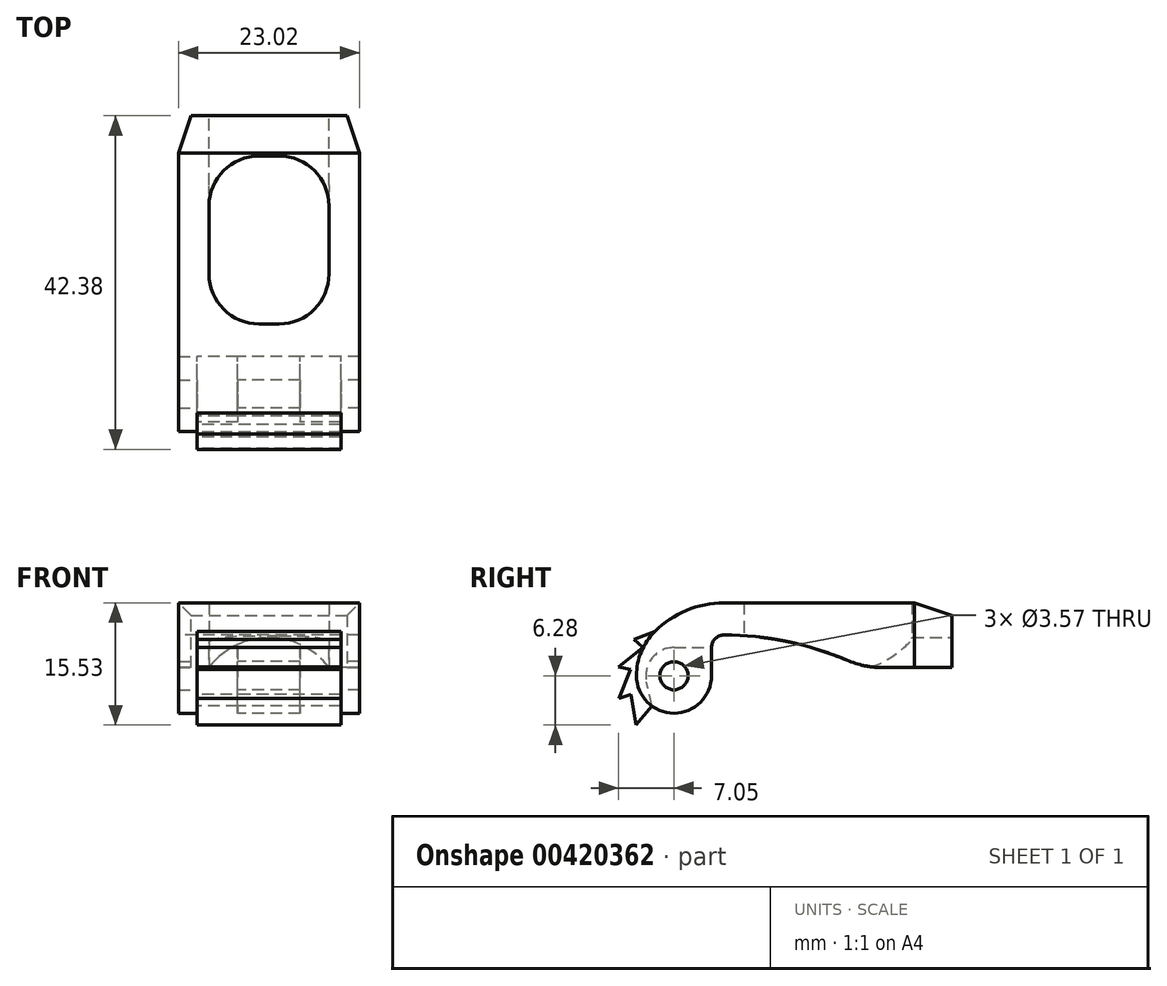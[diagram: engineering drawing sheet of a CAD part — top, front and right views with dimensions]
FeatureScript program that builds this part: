
annotation { "Feature Type Name" : "Feature", "Feature Type Description" : "" }
export const myFeature = defineFeature(function(context is Context, id is Id, definition is map)
    precondition{}
    {
        {
            var Q0;
            Q0=qCreatedBy(makeId("Right.planeOp"),FACE);
            var sketch = newSketch(context, id + "F0", { "sketchPlane" : qUnion([Q0])});
            skCircle(sketch, "E0", {"center": v(0, 0) * mm, "radius": 1.59 * mm, "construction": true});
            skCircle(sketch, "E1", {"center": v(0, 0) * mm, "radius": 1.79 * mm});
            skArc(sketch, "E2", {"start": v(-4.76, 0) * mm, "mid": v(0, -4.76) * mm, "end": v(4.76, 0) * mm});
            skArc(sketch, "E3", {"start": v(-4.76, 0) * mm, "mid": v(-4.16, 3.04) * mm, "end": v(-2.44, 5.61) * mm});
            skArc(sketch, "E4", {"start": v(-2.44, 5.61) * mm, "mid": v(1.6, 8.3) * mm, "end": v(6.35, 9.25) * mm});
            skArc(sketch, "E5", {"start": v(21.93, 1.97) * mm, "mid": v(14.3, 4.35) * mm, "end": v(6.35, 5.16) * mm});
            skLineSegment(sketch, "E6", {"start": v(35.33, 1.03) * mm, "end": v(35.33, 9.25) * mm});
            skLineSegment(sketch, "E7", {"start": v(26.55, 1.03) * mm, "end": v(35.33, 1.03) * mm});
            skArc(sketch, "E8", {"start": v(21.93, 1.97) * mm, "mid": v(24.2, 1.27) * mm, "end": v(26.55, 1.03) * mm});
            skLineSegment(sketch, "E9", {"start": v(6.35, 9.25) * mm, "end": v(6.35, 5.16) * mm});
            skLineSegment(sketch, "E10", {"start": v(6.35, 9.25) * mm, "end": v(35.33, 9.25) * mm});
            skArc(sketch, "E11", {"start": v(6.35, 5.16) * mm, "mid": v(5.23, 4.7) * mm, "end": v(4.76, 3.57) * mm});
            skLineSegment(sketch, "E12", {"start": v(4.76, 0) * mm, "end": v(4.76, 3.57) * mm});
            skLineSegment(sketch, "E13", {"start": v(-2.44, 5.61) * mm, "end": v(3.17, 0) * mm, "construction": true});
            skLineSegment(sketch, "E14", {"start": v(-4.76, 0) * mm, "end": v(3.17, 0) * mm, "construction": true});
            skSolve(sketch);
        }
        {
            var Q0;
            Q0=qCreatedBy(makeId("Right.planeOp"),FACE);
            var sketch = newSketch(context, id + "F1", { "sketchPlane" : qUnion([Q0])});
            skLineSegment(sketch, "E15", {"start": v(-5.46, -2.36) * mm, "end": v(-6.96, -2.88) * mm});
            skLineSegment(sketch, "E16", {"start": v(-5.46, -2.36) * mm, "end": v(-4.85, -6.28) * mm});
            skLineSegment(sketch, "E17", {"start": v(-6.96, -2.88) * mm, "end": v(-4.85, -6.28) * mm, "construction": true});
            skLineSegment(sketch, "E18", {"start": v(-6.96, -2.88) * mm, "end": v(-5.5, 0.81) * mm});
            skLineSegment(sketch, "E19", {"start": v(-5.5, 0.81) * mm, "end": v(-7.05, 1.13) * mm});
            skLineSegment(sketch, "E20", {"start": v(-7.05, 1.13) * mm, "end": v(-3.92, 3.57) * mm});
            skLineSegment(sketch, "E21", {"start": v(-6.96, -2.88) * mm, "end": v(-7.05, 1.13) * mm, "construction": true});
            skLineSegment(sketch, "E22", {"start": v(-3.92, 3.57) * mm, "end": v(-5.1, 4.63) * mm});
            skLineSegment(sketch, "E23", {"start": v(-5.1, 4.63) * mm, "end": v(-7.05, 1.13) * mm, "construction": true});
            skLineSegment(sketch, "E24", {"start": v(-5.46, -2.36) * mm, "end": v(-5.5, 0.81) * mm, "construction": true});
            skLineSegment(sketch, "E25", {"start": v(-5.5, 0.81) * mm, "end": v(-3.92, 3.57) * mm, "construction": true});
            skLineSegment(sketch, "E26", {"start": v(-4.85, -6.28) * mm, "end": v(-3.82, -5.08) * mm});
            skLineSegment(sketch, "E27", {"start": v(-3.82, -5.08) * mm, "end": v(-5.46, -2.36) * mm, "construction": true});
            skLineSegment(sketch, "E28", {"start": v(-3.82, -5.08) * mm, "end": v(-2.78, -3.87) * mm});
            skLineSegment(sketch, "E29", {"start": v(-2.44, 5.61) * mm, "end": v(-5.1, 4.63) * mm});
            skArc(sketch, "E30.0", {"start": v(-4.76, 0) * mm, "mid": v(-4.16, 3.04) * mm, "end": v(-2.44, 5.61) * mm, "construction": true});
            skArc(sketch, "E31.0", {"start": v(-4.76, 0) * mm, "mid": v(-4.24, -2.17) * mm, "end": v(-2.78, -3.87) * mm, "construction": true});
            skArc(sketch, "E32.0", {"start": v(-2.44, 5.61) * mm, "mid": v(1.6, 8.3) * mm, "end": v(6.35, 9.25) * mm});
            skCircle(sketch, "E33.0", {"center": v(0, 0) * mm, "radius": 1.59 * mm, "construction": true});
            skCircle(sketch, "E34.0", {"center": v(0, 0) * mm, "radius": 1.79 * mm});
            skLineSegment(sketch, "E35", {"start": v(-2.78, -3.87) * mm, "end": v(-3.48, -0.8) * mm});
            skLineSegment(sketch, "E36", {"start": v(0, 3.57) * mm, "end": v(4.76, 3.57) * mm});
            skArc(sketch, "E37", {"start": v(-3.48, -0.8) * mm, "mid": v(-2.8, 2.23) * mm, "end": v(0, 3.57) * mm});
            skArc(sketch, "E38", {"start": v(-2.78, -3.87) * mm, "mid": v(2.17, -4.24) * mm, "end": v(4.76, 0) * mm});
            skLineSegment(sketch, "E39", {"start": v(6.35, 9.25) * mm, "end": v(6.35, 9.25) * mm});
            skLineSegment(sketch, "E40.0", {"start": v(6.35, 9.25) * mm, "end": v(6.35, 5.16) * mm});
            skArc(sketch, "E41.0", {"start": v(6.35, 5.16) * mm, "mid": v(5.23, 4.7) * mm, "end": v(4.76, 3.57) * mm});
            skLineSegment(sketch, "E42.0", {"start": v(4.76, 0) * mm, "end": v(4.76, 3.57) * mm});
            skSolve(sketch);
        }
        {
            var Q0;
            Q0=makeQuery(id+"F1.imprint","IMPRINT",FACE,{"disambiguationData":[TD([[makeQuery(id+"F1.imprint","IMPRINT",EDGE,{"derivedFrom":sQuery(id+"F1.wireOp",EDGE,"E34.0")}),-1.0]])]});
            extrude(context, id + "F2", {"entities" : qUnion([Q0]), "endBound" : BoundingType.SYMMETRIC, "depth" : 7.94 * mm});
        }
        {
            var Q0;
            Q0=makeQuery(id+"F1.imprint","IMPRINT",FACE,{"disambiguationData":[TD([[makeQuery(id+"F1.imprint","IMPRINT",EDGE,{"derivedFrom":sQuery(id+"F1.wireOp",EDGE,"E15")}),-1.0]])]});
            extrude(context, id + "F3", {"entities" : qUnion([Q0]), "operationType" : NewBodyOperationType.ADD, "endBound" : BoundingType.SYMMETRIC, "depth" : 18.26 * mm});
        }
        {
            var Q0;
            Q0=makeQuery(id+"F0.imprint","IMPRINT",FACE,{"disambiguationData":[TD([[makeQuery(id+"F0.imprint","IMPRINT",EDGE,{"derivedFrom":sQuery(id+"F0.wireOp",EDGE,"E1")}),-1.0]])]});
            extrude(context, id + "F4", {"entities" : qUnion([Q0]), "depth" : 11.5 * mm, "hasSecondDirection" : true, "secondDirectionOppositeDirection" : false, "secondDirectionDepth" : 9.13 * mm});
        }
        {
            var Q0;
            Q0=makeQuery(id+"F4.opExtrude","SWEPT_BODY",BODY,{"disambiguationData":[OSD([sQuery(id+"F0.wireOp",EDGE,"E1"),sQuery(id+"F0.wireOp",EDGE,"E2"),sQuery(id+"F0.wireOp",EDGE,"E3"),sQuery(id+"F0.wireOp",EDGE,"E4"),sQuery(id+"F0.wireOp",EDGE,"fa3259e1-2bbc-4a5b-8af4-beee35e96bd7"),sQuery(id+"F0.wireOp",EDGE,"0033a4fd-8af5-42d8-bb21-c3096fc00434"),sQuery(id+"F0.wireOp",EDGE,"SGoBp1ZG-taL4-AfqJ-2I2P-gVCW2I0r0lYD"),sQuery(id+"F0.wireOp",EDGE,"iwrRzGqT-2APR-WYXl-iObo-SlBq5ROOTsbk"),sQuery(id+"F0.wireOp",EDGE,"a1e60f74-6165-4a4e-a639-ccb8da934d98"),sQuery(id+"F0.wireOp",EDGE,"E5"),sQuery(id+"F0.wireOp",EDGE,"2cBdYGLl-GkL6-4I3l-MRBm-wGwyNUsLkLAq"),sQuery(id+"F0.wireOp",EDGE,"3e1c12e4-8fd2-4ef8-b60a-6f2414db5ed0"),sQuery(id+"F0.wireOp",EDGE,"VwxYTSdr-CvJO-G9BG-kuss-uXTzOh8zcSg1")])]});
            var Q1;
            Q1=qCreatedBy(makeId("Right.planeOp"),FACE);
            mirror(context, id + "F5", {"entities" : qUnion([Q0]), "mirrorPlane" : qUnion([Q1])});
        }
        {
            var Q0;
            Q0=qCreatedBy(makeId("Top.planeOp"),FACE);
            var sketch = newSketch(context, id + "F6", { "sketchPlane" : qUnion([Q0])});
            skLineSegment(sketch, "E43.bottom", {"start": v(-7.62, 30.23) * mm, "end": v(7.62, 30.23) * mm});
            skLineSegment(sketch, "E43.top", {"start": v(-7.62, 8.89) * mm, "end": v(7.62, 8.9) * mm});
            skLineSegment(sketch, "E43.left", {"start": v(-7.62, 30.23) * mm, "end": v(-7.62, 8.89) * mm});
            skLineSegment(sketch, "E43.right", {"start": v(7.62, 30.23) * mm, "end": v(7.62, 8.89) * mm});
            skPoint(sketch, "E44", {"position": v(0, 8.9) * mm});
            skLineSegment(sketch, "E45.0", {"start": v(-3.97, 4.76) * mm, "end": v(-9.13, 4.76) * mm, "construction": true});
            skLineSegment(sketch, "E46.0", {"start": v(3.97, 4.76) * mm, "end": v(-3.97, 4.76) * mm, "construction": true});
            skLineSegment(sketch, "E47.0", {"start": v(9.13, 4.76) * mm, "end": v(3.97, 4.76) * mm, "construction": true});
            skSolve(sketch);
        }
        {
            var Q0;
            Q0=makeQuery(id+"F0.imprint","IMPRINT",FACE,{"disambiguationData":[TD([[makeQuery(id+"F0.imprint","IMPRINT",EDGE,{"derivedFrom":sQuery(id+"F0.wireOp",EDGE,"fa3259e1-2bbc-4a5b-8af4-beee35e96bd7")}),-1.0]])]});
            var Q1;
            Q1=makeQuery(id+"F0.imprint","IMPRINT",FACE,{"disambiguationData":[TD([[makeQuery(id+"F0.imprint","IMPRINT",EDGE,{"derivedFrom":sQuery(id+"F0.wireOp",EDGE,"E6")}),1.0]])]});
            extrude(context, id + "F7", {"entities" : qUnion([Q0, Q1]), "operationType" : NewBodyOperationType.ADD, "endBound" : BoundingType.SYMMETRIC, "depth" : 23.02 * mm});
        }
        {
            var Q0;
            Q0 = qSketchRegion(id + "F6", true);
            extrude(context, id + "F8", {"entities" : qUnion([Q0]), "operationType" : NewBodyOperationType.REMOVE, "endBound" : BoundingType.THROUGH_ALL, "depth" : 25.4 * mm});
        }
        {
            var Q0;
            Q0=makeQuery(id+"F8.boolean.opBoolean","COPY",EDGE,{"derivedFrom":makeQuery(id+"F8.opExtrude","SWEPT_EDGE",EDGE,{"disambiguationData":[OSD([sQuery(id+"F6.wireOp",EDGE,"E43.bottom"),sQuery(id+"F6.wireOp",EDGE,"E43.left")])]})});
            var Q1;
            Q1=makeQuery(id+"F8.boolean.opBoolean","COPY",EDGE,{"derivedFrom":makeQuery(id+"F8.opExtrude","SWEPT_EDGE",EDGE,{"disambiguationData":[OSD([sQuery(id+"F6.wireOp",EDGE,"E43.bottom"),sQuery(id+"F6.wireOp",EDGE,"E43.right")])]})});
            var Q2;
            Q2=makeQuery(id+"F8.boolean.opBoolean","COPY",EDGE,{"derivedFrom":makeQuery(id+"F8.opExtrude","SWEPT_EDGE",EDGE,{"disambiguationData":[OSD([sQuery(id+"F6.wireOp",EDGE,"E43.top"),sQuery(id+"F6.wireOp",EDGE,"E43.right")])]})});
            var Q3;
            Q3=makeQuery(id+"F8.boolean.opBoolean","COPY",EDGE,{"derivedFrom":makeQuery(id+"F8.opExtrude","SWEPT_EDGE",EDGE,{"disambiguationData":[OSD([sQuery(id+"F6.wireOp",EDGE,"E43.top"),sQuery(id+"F6.wireOp",EDGE,"E43.left")])]})});
            fillet(context, id + "F9", {"entities" : qUnion([Q0, Q1, Q2, Q3]), "radius" : 6.35 * mm, "tangentPropagation" : true, "allowEdgeOverflow" : false});
        }
        {
            var Q0;
            Q0=makeQuery(id+"F7.opExtrude","SWEPT_FACE",FACE,{"disambiguationData":[OSD([sQuery(id+"F0.wireOp",EDGE,"E6"),sQuery(id+"F0.wireOp",EDGE,"d5pfMPTk-49E0-qcFO-zJr8-5D5xXmkC3dLN")])]});
            var sketch = newSketch(context, id + "F10", { "sketchPlane" : qUnion([Q0])});
            skLineSegment(sketch, "E48.0", {"start": v(7.62, 0) * mm, "end": v(-7.62, 0) * mm, "construction": true});
            skLineSegment(sketch, "E49.0", {"start": v(-11.5, 1.03) * mm, "end": v(11.5, 1.03) * mm, "construction": true});
            skLineSegment(sketch, "E50.0", {"start": v(-11.5, 9.25) * mm, "end": v(11.5, 9.25) * mm, "construction": true});
            skLineSegment(sketch, "E51.0", {"start": v(-11.5, 1.03) * mm, "end": v(-11.5, 9.25) * mm, "construction": true});
            skLineSegment(sketch, "E52.0", {"start": v(11.5, 1.03) * mm, "end": v(11.5, 9.25) * mm, "construction": true});
            skArc(sketch, "E53", {"start": v(7.62, 1.03) * mm, "mid": v(0, 4.84) * mm, "end": v(-7.62, 1.03) * mm});
            skLineSegment(sketch, "E54", {"start": v(-7.62, 1.03) * mm, "end": v(7.62, 1.03) * mm});
            skSolve(sketch);
        }
        {
            var Q0;
            Q0=makeQuery(id+"F10.imprint","IMPRINT",FACE,{"disambiguationData":[TD([[makeQuery(id+"F10.imprint","IMPRINT",EDGE,{"derivedFrom":sQuery(id+"F10.wireOp",EDGE,"E53")}),1.0]])]});
            var Q1;
            {var subQ0=makeQuery(id+"F4.opExtrude","SWEPT_FACE",FACE,{"disambiguationData":[OSD([sQuery(id+"F0.wireOp",EDGE,"E11")])]});Q1=makeQuery(id+"F7.boolean.opBoolean","MERGE",FACE,{"derivedFrom":[makeQuery(id+"F3.opExtrude","SWEPT_FACE",FACE,{"disambiguationData":[OSD([sQuery(id+"F1.wireOp",EDGE,"E41.0")])]}),subQ0,makeQuery(id+"F5.opPattern","COPY",FACE,{"derivedFrom":subQ0,"instanceName":"1"})]});}
            extrude(context, id + "F11", {"entities" : qUnion([Q0]), "operationType" : NewBodyOperationType.REMOVE, "endBound" : BoundingType.UP_TO_NEXT, "oppositeDirection" : true, "endBoundEntityFace" : qUnion([Q1]), "depth" : 25.4 * mm});
        }
        {
            var Q0;
            Q0=makeQuery(id+"F7.opExtrude","CAP_EDGE",EDGE,{"disambiguationData":[OSD([sQuery(id+"F0.wireOp",EDGE,"E6"),sQuery(id+"F0.wireOp",EDGE,"d5pfMPTk-49E0-qcFO-zJr8-5D5xXmkC3dLN")])],"isStart":false});
            var Q1;
            Q1=makeQuery(id+"F7.opExtrude","SWEPT_EDGE",EDGE,{"disambiguationData":[OSD([sQuery(id+"F0.wireOp",EDGE,"d5pfMPTk-49E0-qcFO-zJr8-5D5xXmkC3dLN"),sQuery(id+"F0.wireOp",EDGE,"E10")])]});
            var Q2;
            Q2=makeQuery(id+"F7.opExtrude","CAP_EDGE",EDGE,{"disambiguationData":[OSD([sQuery(id+"F0.wireOp",EDGE,"E6"),sQuery(id+"F0.wireOp",EDGE,"d5pfMPTk-49E0-qcFO-zJr8-5D5xXmkC3dLN")])],"isStart":true});
            chamfer(context, id + "F12", {"entities" : qUnion([Q0, Q1, Q2]), "chamferType" : ChamferType.TWO_OFFSETS, "width1" : 1.59 * mm, "oppositeDirection" : true, "width2" : 4.76 * mm, "tangentPropagation" : true});
        }
    });
